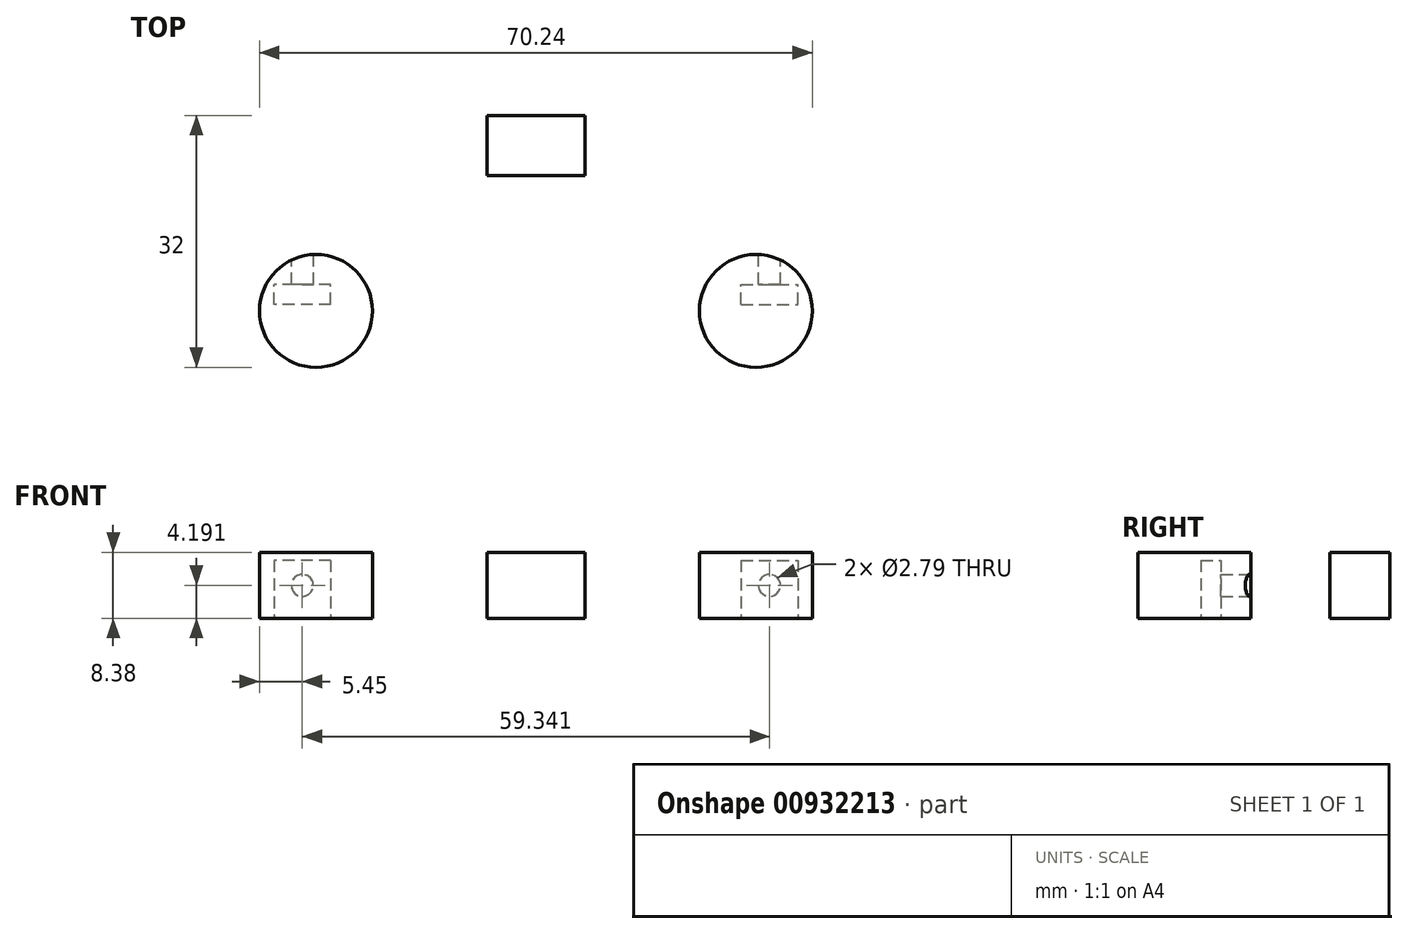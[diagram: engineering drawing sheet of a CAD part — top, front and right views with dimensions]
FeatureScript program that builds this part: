
annotation { "Feature Type Name" : "Feature", "Feature Type Description" : "" }
export const myFeature = defineFeature(function(context is Context, id is Id, definition is map)
    precondition{}
    {
        {
            var Q0;
            Q0=qCreatedBy(makeId("Top.planeOp"),FACE);
            var sketch = newSketch(context, id + "F0", { "sketchPlane" : qUnion([Q0])});
            skLineSegment(sketch, "E0", {"start": v(0, 0) * mm, "end": v(35.12, 0) * mm});
            skLineSegment(sketch, "E1", {"start": v(0, 0) * mm, "end": v(-35.12, 0) * mm});
            skLineSegment(sketch, "E2", {"start": v(0, 0) * mm, "end": v(0, -32) * mm});
            skLineSegment(sketch, "E3", {"start": v(0, 0) * mm, "end": v(0, -14.48) * mm});
            skLineSegment(sketch, "E4", {"start": v(0, -14.48) * mm, "end": v(-34.5, -14.48) * mm});
            skLineSegment(sketch, "E5", {"start": v(0, -14.48) * mm, "end": v(34.5, -14.48) * mm});
            skLineSegment(sketch, "E6", {"start": v(35.12, 0) * mm, "end": v(35.12, -32) * mm});
            skLineSegment(sketch, "E7", {"start": v(-35.12, 0) * mm, "end": v(-35.12, -32) * mm});
            skLineSegment(sketch, "E8", {"start": v(-35.12, -32) * mm, "end": v(35.12, -32) * mm});
            skLineSegment(sketch, "E9", {"start": v(-34.5, -14.48) * mm, "end": v(-35.12, -14.48) * mm});
            skLineSegment(sketch, "E10", {"start": v(-35.12, -14.48) * mm, "end": v(-35.12, -13.82) * mm});
            skLineSegment(sketch, "E11", {"start": v(-35.12, -14.48) * mm, "end": v(-35.12, -15.14) * mm});
            skLineSegment(sketch, "E12", {"start": v(-35.12, -13.82) * mm, "end": v(-34.5, -14.48) * mm});
            skLineSegment(sketch, "E13", {"start": v(-35.12, -15.14) * mm, "end": v(-34.5, -14.48) * mm});
            skLineSegment(sketch, "E14", {"start": v(35.12, -15.14) * mm, "end": v(34.5, -14.48) * mm});
            skLineSegment(sketch, "E15", {"start": v(34.5, -14.48) * mm, "end": v(35.12, -13.82) * mm});
            skLineSegment(sketch, "E16", {"start": v(35.12, -13.82) * mm, "end": v(35.12, -14.48) * mm});
            skLineSegment(sketch, "E17", {"start": v(35.12, -14.48) * mm, "end": v(35.12, -15.14) * mm});
            skLineSegment(sketch, "E18", {"start": v(0, -32) * mm, "end": v(-27.94, -32) * mm});
            skLineSegment(sketch, "E19", {"start": v(0, -32) * mm, "end": v(27.94, -32) * mm});
            skLineSegment(sketch, "E20", {"start": v(-27.94, -32) * mm, "end": v(-27.94, -24.83) * mm});
            skLineSegment(sketch, "E21", {"start": v(27.94, -32) * mm, "end": v(27.94, -24.83) * mm});
            skCircle(sketch, "E22", {"center": v(-27.94, -24.83) * mm, "radius": 7.18 * mm});
            skCircle(sketch, "E23", {"center": v(27.94, -24.83) * mm, "radius": 7.18 * mm});
            skLineSegment(sketch, "E24", {"start": v(0, 0) * mm, "end": v(-6.22, 0) * mm});
            skLineSegment(sketch, "E25", {"start": v(0, 0) * mm, "end": v(6.22, 0) * mm});
            skLineSegment(sketch, "E26", {"start": v(-6.22, 0) * mm, "end": v(-6.22, -7.62) * mm});
            skLineSegment(sketch, "E27", {"start": v(-6.22, -7.62) * mm, "end": v(6.22, -7.62) * mm});
            skLineSegment(sketch, "E28.bottom", {"start": v(6.22, 0) * mm, "end": v(-6.22, 0) * mm});
            skLineSegment(sketch, "E28.top", {"start": v(6.22, -7.62) * mm, "end": v(-6.22, -7.62) * mm});
            skLineSegment(sketch, "E28.left", {"start": v(6.22, 0) * mm, "end": v(6.22, -7.62) * mm});
            skSolve(sketch);
        }
        {
            var Q0;
            {var subQ1=sQuery(id+"F0.wireOp",EDGE,"E1");Q0=makeQuery(id+"F0.imprint","IMPRINT",FACE,{"disambiguationData":[TD([[makeQuery(id+"F0.imprint","IMPRINT",EDGE,{"derivedFrom":subQ1}),1.0]])]});}
            var Q1;
            {var subQ1=sQuery(id+"F0.wireOp",EDGE,"E0");Q1=makeQuery(id+"F0.imprint","IMPRINT",FACE,{"disambiguationData":[TD([[makeQuery(id+"F0.imprint","IMPRINT",EDGE,{"derivedFrom":subQ1}),-1.0]])]});}
            extrude(context, id + "F1", {"entities" : qUnion([Q0, Q1]), "depth" : 8.38 * mm, "offsetDistance" : 25.4 * mm});
        }
        {
            var Q0;
            Q0=makeQuery(id+"F0.imprint","IMPRINT",FACE,{"disambiguationData":[TD([[makeQuery(id+"F0.imprint","IMPRINT",EDGE,{"derivedFrom":sQuery(id+"F0.wireOp",EDGE,"E2")}),-1.0]])]});
            var Q1;
            {var subQ0=sQuery(id+"F0.wireOp",EDGE,"E22");var subQ2=makeQuery(id+"F0.imprint","INTERSECT",VERTEX,{"derivedFrom":[sQuery(id+"F0.wireOp",EDGE,"E7"),subQ0]});Q1=makeQuery(id+"F0.imprint","IMPRINT",FACE,{"disambiguationData":[TD([[makeQuery(id+"F0.imprint","IMPRINT",EDGE,{"disambiguationData":[TD([[subQ2,-1.0]])],"derivedFrom":subQ0}),1.0]])]});}
            var Q2;
            Q2=makeQuery(id+"F0.imprint","IMPRINT",FACE,{"disambiguationData":[TD([[makeQuery(id+"F0.imprint","IMPRINT",EDGE,{"derivedFrom":sQuery(id+"F0.wireOp",EDGE,"E2")}),1.0]])]});
            var Q3;
            {var subQ0=sQuery(id+"F0.wireOp",EDGE,"E23");var subQ2=makeQuery(id+"F0.imprint","INTERSECT",VERTEX,{"derivedFrom":[sQuery(id+"F0.wireOp",EDGE,"E6"),subQ0]});Q3=makeQuery(id+"F0.imprint","IMPRINT",FACE,{"disambiguationData":[TD([[makeQuery(id+"F0.imprint","IMPRINT",EDGE,{"disambiguationData":[TD([[subQ2,-1.0]])],"derivedFrom":subQ0}),1.0]])]});}
            extrude(context, id + "F2", {"entities" : qUnion([Q0, Q1, Q2, Q3]), "depth" : 8.38 * mm, "offsetDistance" : 25.4 * mm});
        }
        {
            var Q0;
            Q0=makeQuery(id+"F1.opExtrude","CAP_FACE",FACE,{"disambiguationData":[OSD([sQuery(id+"F0.wireOp",EDGE,"E0"),sQuery(id+"F0.wireOp",EDGE,"E1"),sQuery(id+"F0.wireOp",EDGE,"E4"),sQuery(id+"F0.wireOp",EDGE,"E5"),sQuery(id+"F0.wireOp",EDGE,"E6"),sQuery(id+"F0.wireOp",EDGE,"E7"),sQuery(id+"F0.wireOp",EDGE,"E12"),sQuery(id+"F0.wireOp",EDGE,"E15"),sQuery(id+"F0.wireOp",EDGE,"E28.top"),sQuery(id+"F0.wireOp",EDGE,"E28.left"),sQuery(id+"F0.wireOp",EDGE,"E26")])],"isStart":false});
            var sketch = newSketch(context, id + "F3", { "sketchPlane" : qUnion([Q0])});
            skLineSegment(sketch, "E29", {"start": v(0, -14.48) * mm, "end": v(0, 0) * mm});
            skLineSegment(sketch, "E30", {"start": v(0, 0) * mm, "end": v(35.12, 0) * mm});
            skLineSegment(sketch, "E31", {"start": v(17.56, 0) * mm, "end": v(17.56, -14.48) * mm});
            skLineSegment(sketch, "E32", {"start": v(17.56, -14.48) * mm, "end": v(0, -14.48) * mm});
            skLineSegment(sketch, "E33", {"start": v(35.12, 0) * mm, "end": v(35.12, -14.48) * mm});
            skLineSegment(sketch, "E34", {"start": v(35.12, -14.48) * mm, "end": v(17.56, -14.48) * mm});
            skLineSegment(sketch, "E35", {"start": v(17.56, -14.48) * mm, "end": v(24.23, -14.48) * mm});
            skLineSegment(sketch, "E36", {"start": v(17.56, -14.48) * mm, "end": v(10.9, -14.48) * mm});
            skLineSegment(sketch, "E37", {"start": v(10.9, -14.48) * mm, "end": v(10.9, -11.6) * mm});
            skLineSegment(sketch, "E38", {"start": v(24.23, -14.48) * mm, "end": v(24.23, -17.35) * mm});
            skLineSegment(sketch, "E39.bottom", {"start": v(10.9, -11.6) * mm, "end": v(24.23, -11.6) * mm});
            skLineSegment(sketch, "E39.top", {"start": v(10.9, -17.35) * mm, "end": v(24.23, -17.35) * mm});
            skLineSegment(sketch, "E39.left", {"start": v(10.9, -11.6) * mm, "end": v(10.9, -17.35) * mm});
            skLineSegment(sketch, "E39.right", {"start": v(24.23, -11.6) * mm, "end": v(24.23, -17.35) * mm});
            skSolve(sketch);
        }
        {
            var Q0;
            {var subQ5=sQuery(id+"F3.wireOp",EDGE,"E37");Q0=makeQuery(id+"F3.imprint","IMPRINT",FACE,{"disambiguationData":[TD([[makeQuery(id+"F3.imprint","IMPRINT",EDGE,{"derivedFrom":subQ5}),-1.0]])]});}
            var Q1;
            {var subQ5=sQuery(id+"F3.wireOp",EDGE,"E39.right");Q1=makeQuery(id+"F3.imprint","IMPRINT",FACE,{"disambiguationData":[TD([[makeQuery(id+"F3.imprint","IMPRINT",EDGE,{"derivedFrom":subQ5}),-1.0]])]});}
            var Q2;
            {var subQ4=sQuery(id+"F3.wireOp",EDGE,"E38");Q2=makeQuery(id+"F3.imprint","IMPRINT",FACE,{"disambiguationData":[TD([[makeQuery(id+"F3.imprint","IMPRINT",EDGE,{"derivedFrom":subQ4}),-1.0]])]});}
            var Q3;
            Q3=makeQuery(id+"F2.opExtrude","CAP_FACE",FACE,{"disambiguationData":[OSD([sQuery(id+"F0.wireOp",EDGE,"E4"),sQuery(id+"F0.wireOp",EDGE,"E5"),sQuery(id+"F0.wireOp",EDGE,"E6"),sQuery(id+"F0.wireOp",EDGE,"E7"),sQuery(id+"F0.wireOp",EDGE,"E13"),sQuery(id+"F0.wireOp",EDGE,"E14"),sQuery(id+"F0.wireOp",EDGE,"E18"),sQuery(id+"F0.wireOp",EDGE,"E19"),sQuery(id+"F0.wireOp",EDGE,"E22"),sQuery(id+"F0.wireOp",EDGE,"E23")])],"isStart":true});
            extrude(context, id + "F4", {"entities" : qUnion([Q0, Q1, Q2]), "operationType" : NewBodyOperationType.REMOVE, "oppositeDirection" : true, "depth" : 25.4 * mm, "endBoundEntityFace" : qUnion([Q3]), "offsetDistance" : 25.4 * mm});
        }
        {
            var Q0;
            Q0=qCreatedBy(makeId("Top.planeOp"),FACE);
            var sketch = newSketch(context, id + "F5", { "sketchPlane" : qUnion([Q0])});
            skLineSegment(sketch, "E40", {"start": v(0, 0) * mm, "end": v(35.12, 0) * mm});
            skLineSegment(sketch, "E41", {"start": v(17.56, 0) * mm, "end": v(17.56, -14.48) * mm});
            skLineSegment(sketch, "E42", {"start": v(17.56, -14.48) * mm, "end": v(24.23, -14.48) * mm});
            skLineSegment(sketch, "E43", {"start": v(35.12, 0) * mm, "end": v(35.12, -14.48) * mm});
            skLineSegment(sketch, "E44", {"start": v(35.12, -14.48) * mm, "end": v(24.23, -14.48) * mm});
            skLineSegment(sketch, "E45", {"start": v(24.23, -14.48) * mm, "end": v(35.12, -14.48) * mm});
            skLineSegment(sketch, "E46", {"start": v(29.67, -14.48) * mm, "end": v(29.67, -4.95) * mm});
            skLineSegment(sketch, "E47", {"start": v(29.67, -14.48) * mm, "end": v(29.67, -24) * mm});
            skLineSegment(sketch, "E48", {"start": v(29.67, -24) * mm, "end": v(26.05, -24) * mm});
            skLineSegment(sketch, "E49", {"start": v(29.67, -24) * mm, "end": v(29.67, -21.46) * mm});
            skLineSegment(sketch, "E50.bottom", {"start": v(26.05, -24) * mm, "end": v(33.29, -24) * mm});
            skLineSegment(sketch, "E50.top", {"start": v(26.05, -21.46) * mm, "end": v(33.29, -21.46) * mm});
            skLineSegment(sketch, "E50.left", {"start": v(26.05, -24) * mm, "end": v(26.05, -21.46) * mm});
            skLineSegment(sketch, "E50.right", {"start": v(33.29, -24) * mm, "end": v(33.29, -21.46) * mm});
            skPoint(sketch, "E50.middle", {"position": v(29.67, -22.73) * mm});
            skLineSegment(sketch, "E51", {"start": v(29.67, -22.73) * mm, "end": v(0, -22.73) * mm});
            skLineSegment(sketch, "E52", {"start": v(0, -22.73) * mm, "end": v(-29.67, -22.73) * mm});
            skLineSegment(sketch, "E53", {"start": v(26.05, -24) * mm, "end": v(0, -24) * mm});
            skLineSegment(sketch, "E54", {"start": v(0, -24) * mm, "end": v(-26.05, -24) * mm});
            skLineSegment(sketch, "E55.bottom", {"start": v(-26.05, -24) * mm, "end": v(-33.29, -24) * mm});
            skLineSegment(sketch, "E55.top", {"start": v(-26.05, -21.46) * mm, "end": v(-33.29, -21.46) * mm});
            skLineSegment(sketch, "E55.left", {"start": v(-26.05, -24) * mm, "end": v(-26.05, -21.46) * mm});
            skLineSegment(sketch, "E55.right", {"start": v(-33.29, -24) * mm, "end": v(-33.29, -21.46) * mm});
            skPoint(sketch, "E55.middle", {"position": v(-29.67, -22.73) * mm});
            skLineSegment(sketch, "E56", {"start": v(29.67, -4.95) * mm, "end": v(29.67, 0) * mm});
            skSolve(sketch);
        }
        {
            var Q0;
            {var subQ4=sQuery(id+"F5.wireOp",EDGE,"E50.bottom");Q0=makeQuery(id+"F5.imprint","IMPRINT",FACE,{"disambiguationData":[TD([[makeQuery(id+"F5.imprint","IMPRINT",EDGE,{"derivedFrom":subQ4}),1.0]])]});}
            var Q1;
            {var subQ0=sQuery(id+"F5.wireOp",EDGE,"E50.top");var subQ1=sQuery(id+"F5.wireOp",EDGE,"E47");var subQ2=makeQuery(id+"F5.imprint","INTERSECT",VERTEX,{"derivedFrom":[subQ1,subQ0]});Q1=makeQuery(id+"F5.imprint","IMPRINT",FACE,{"disambiguationData":[TD([[makeQuery(id+"F5.imprint","IMPRINT",EDGE,{"disambiguationData":[TD([[subQ2,-1.0]])],"derivedFrom":subQ1}),-1.0]])]});}
            var Q2;
            {var subQ0=sQuery(id+"F5.wireOp",EDGE,"E48");Q2=makeQuery(id+"F5.imprint","IMPRINT",FACE,{"disambiguationData":[TD([[makeQuery(id+"F5.imprint","IMPRINT",EDGE,{"derivedFrom":subQ0}),-1.0]])]});}
            var Q3;
            {var subQ1=sQuery(id+"F5.wireOp",EDGE,"E55.bottom");Q3=makeQuery(id+"F5.imprint","IMPRINT",FACE,{"disambiguationData":[TD([[makeQuery(id+"F5.imprint","IMPRINT",EDGE,{"derivedFrom":subQ1}),-1.0]])]});}
            extrude(context, id + "F6", {"entities" : qUnion([Q0, Q1, Q2, Q3]), "operationType" : NewBodyOperationType.REMOVE, "depth" : 7.37 * mm, "offsetDistance" : 25.4 * mm});
        }
        {
            var Q0;
            Q0=makeQuery(id+"F1.opExtrude","SWEPT_FACE",FACE,{"disambiguationData":[OSD([sQuery(id+"F0.wireOp",EDGE,"E0")])]});
            var sketch = newSketch(context, id + "F7", { "sketchPlane" : qUnion([Q0])});
            skLineSegment(sketch, "E57", {"start": v(-35.12, 0) * mm, "end": v(-29.67, 0) * mm});
            skLineSegment(sketch, "E58", {"start": v(-29.67, 0) * mm, "end": v(-29.67, 8.38) * mm});
            skCircle(sketch, "E59", {"center": v(-29.67, 4.2) * mm, "radius": 1.4 * mm});
            skLineSegment(sketch, "E60", {"start": v(-29.67, 4.2) * mm, "end": v(0, 4.2) * mm});
            skLineSegment(sketch, "E61", {"start": v(0, 4.2) * mm, "end": v(29.67, 4.2) * mm});
            skCircle(sketch, "E62", {"center": v(29.67, 4.2) * mm, "radius": 1.4 * mm});
            skCircle(sketch, "E63", {"center": v(-29.67, 4.2) * mm, "radius": 2.67 * mm});
            skCircle(sketch, "E64", {"center": v(29.67, 4.2) * mm, "radius": 2.67 * mm});
            skSolve(sketch);
        }
        {
            var Q0;
            {var subQ0=sQuery(id+"F7.wireOp",EDGE,"E60");var subQ1=sQuery(id+"F7.wireOp",EDGE,"E58");var subQ2=makeQuery(id+"F7.imprint","INTERSECT",VERTEX,{"derivedFrom":[subQ1,subQ0]});Q0=makeQuery(id+"F7.imprint","IMPRINT",FACE,{"disambiguationData":[TD([[makeQuery(id+"F7.imprint","IMPRINT",EDGE,{"disambiguationData":[TD([[subQ2,1.0]])],"derivedFrom":subQ1}),-1.0]])]});}
            var Q1;
            {var subQ0=sQuery(id+"F7.wireOp",EDGE,"E60");var subQ1=sQuery(id+"F7.wireOp",EDGE,"E58");var subQ2=makeQuery(id+"F7.imprint","INTERSECT",VERTEX,{"derivedFrom":[subQ1,subQ0]});Q1=makeQuery(id+"F7.imprint","IMPRINT",FACE,{"disambiguationData":[TD([[makeQuery(id+"F7.imprint","IMPRINT",EDGE,{"disambiguationData":[TD([[subQ2,-1.0]])],"derivedFrom":subQ1}),-1.0]])]});}
            var Q2;
            {var subQ0=sQuery(id+"F7.wireOp",EDGE,"E58");var subQ1=makeQuery(id+"F7.imprint","INTERSECT",VERTEX,{"derivedFrom":[subQ0,sQuery(id+"F7.wireOp",EDGE,"E60")]});Q2=makeQuery(id+"F7.imprint","IMPRINT",FACE,{"disambiguationData":[TD([[makeQuery(id+"F7.imprint","IMPRINT",EDGE,{"disambiguationData":[TD([[subQ1,1.0]])],"derivedFrom":subQ0}),1.0]])]});}
            var Q3;
            Q3=makeQuery(id+"F7.imprint","IMPRINT",FACE,{"disambiguationData":[TD([[makeQuery(id+"F7.imprint","IMPRINT",EDGE,{"derivedFrom":sQuery(id+"F7.wireOp",EDGE,"E62")}),1.0]])]});
            extrude(context, id + "F8", {"entities" : qUnion([Q0, Q1, Q2, Q3]), "operationType" : NewBodyOperationType.REMOVE, "oppositeDirection" : true, "depth" : 24 * mm, "offsetDistance" : 25.4 * mm});
        }
        {
            var Q0;
            {var subQ0=sQuery(id+"F7.wireOp",EDGE,"E59");var subQ1=sQuery(id+"F7.wireOp",EDGE,"E58");var subQ2=makeQuery(id+"F7.imprint","INTERSECT",VERTEX,{"disambiguationData":[OD(1.0)],"derivedFrom":[subQ1,subQ0]});Q0=makeQuery(id+"F7.imprint","IMPRINT",FACE,{"disambiguationData":[TD([[makeQuery(id+"F7.imprint","IMPRINT",EDGE,{"disambiguationData":[TD([[subQ2,-1.0]])],"derivedFrom":subQ1}),-1.0]])]});}
            var Q1;
            {var subQ0=sQuery(id+"F7.wireOp",EDGE,"E63");var subQ1=sQuery(id+"F7.wireOp",EDGE,"E58");var subQ2=makeQuery(id+"F7.imprint","INTERSECT",VERTEX,{"disambiguationData":[OD(0.0)],"derivedFrom":[subQ1,subQ0]});Q1=makeQuery(id+"F7.imprint","IMPRINT",FACE,{"disambiguationData":[TD([[makeQuery(id+"F7.imprint","IMPRINT",EDGE,{"disambiguationData":[TD([[subQ2,-1.0]])],"derivedFrom":subQ1}),1.0]])]});}
            var Q2;
            {var subQ0=sQuery(id+"F7.wireOp",EDGE,"E63");var subQ1=sQuery(id+"F7.wireOp",EDGE,"E58");var subQ2=makeQuery(id+"F7.imprint","INTERSECT",VERTEX,{"disambiguationData":[OD(0.0)],"derivedFrom":[subQ1,subQ0]});Q2=makeQuery(id+"F7.imprint","IMPRINT",FACE,{"disambiguationData":[TD([[makeQuery(id+"F7.imprint","IMPRINT",EDGE,{"disambiguationData":[TD([[subQ2,-1.0]])],"derivedFrom":subQ1}),-1.0]])]});}
            var Q3;
            Q3=makeQuery(id+"F7.imprint","IMPRINT",FACE,{"disambiguationData":[TD([[makeQuery(id+"F7.imprint","IMPRINT",EDGE,{"derivedFrom":sQuery(id+"F7.wireOp",EDGE,"E62")}),-1.0]])]});
            extrude(context, id + "F9", {"entities" : qUnion([Q0, Q1, Q2, Q3]), "operationType" : NewBodyOperationType.REMOVE, "oppositeDirection" : true, "depth" : 4.95 * mm, "offsetDistance" : 25.4 * mm});
        }
        {
            var Q0;
            Q0=makeQuery(id+"F2.opExtrude","CAP_FACE",FACE,{"disambiguationData":[OSD([sQuery(id+"F0.wireOp",EDGE,"E4"),sQuery(id+"F0.wireOp",EDGE,"E5"),sQuery(id+"F0.wireOp",EDGE,"E6"),sQuery(id+"F0.wireOp",EDGE,"E7"),sQuery(id+"F0.wireOp",EDGE,"E13"),sQuery(id+"F0.wireOp",EDGE,"E14"),sQuery(id+"F0.wireOp",EDGE,"E18"),sQuery(id+"F0.wireOp",EDGE,"E19"),sQuery(id+"F0.wireOp",EDGE,"E22"),sQuery(id+"F0.wireOp",EDGE,"E23")])],"isStart":false});
            var sketch = newSketch(context, id + "F10", { "sketchPlane" : qUnion([Q0])});
            skLineSegment(sketch, "E65", {"start": v(10.9, -14.48) * mm, "end": v(24.23, -14.48) * mm});
            skLineSegment(sketch, "E66", {"start": v(17.56, -14.48) * mm, "end": v(10.32, -14.48) * mm});
            skLineSegment(sketch, "E67", {"start": v(17.56, -14.48) * mm, "end": v(24.8, -14.48) * mm});
            skLineSegment(sketch, "E68", {"start": v(17.56, -14.48) * mm, "end": v(17.56, -18.03) * mm});
            skLineSegment(sketch, "E69", {"start": v(17.56, -14.48) * mm, "end": v(17.56, -10.92) * mm});
            skLineSegment(sketch, "E70", {"start": v(17.56, -10.92) * mm, "end": v(11.72, -10.92) * mm});
            skLineSegment(sketch, "E71", {"start": v(17.56, -18.03) * mm, "end": v(23.4, -18.03) * mm});
            skLineSegment(sketch, "E72.bottom", {"start": v(11.72, -10.92) * mm, "end": v(23.4, -10.92) * mm});
            skLineSegment(sketch, "E72.top", {"start": v(11.72, -18.03) * mm, "end": v(23.4, -18.03) * mm});
            skLineSegment(sketch, "E72.left", {"start": v(11.72, -10.92) * mm, "end": v(11.72, -18.03) * mm});
            skLineSegment(sketch, "E72.right", {"start": v(23.4, -10.92) * mm, "end": v(23.4, -18.03) * mm});
            skPoint(sketch, "E72.middle", {"position": v(17.56, -14.48) * mm});
            skLineSegment(sketch, "E73", {"start": v(24.8, -14.48) * mm, "end": v(24.8, -16.38) * mm});
            skLineSegment(sketch, "E74.bottom", {"start": v(24.8, -16.38) * mm, "end": v(10.32, -16.38) * mm});
            skLineSegment(sketch, "E74.top", {"start": v(24.8, -12.57) * mm, "end": v(10.32, -12.57) * mm});
            skLineSegment(sketch, "E74.left", {"start": v(24.8, -16.38) * mm, "end": v(24.8, -12.57) * mm});
            skLineSegment(sketch, "E74.right", {"start": v(10.32, -16.38) * mm, "end": v(10.32, -12.57) * mm});
            skSolve(sketch);
        }
        {
            var Q0;
            {var subQ7=sQuery(id+"F10.wireOp",EDGE,"E66");Q0=makeQuery(id+"F10.imprint","IMPRINT",FACE,{"disambiguationData":[TD([[makeQuery(id+"F10.imprint","IMPRINT",EDGE,{"derivedFrom":subQ7}),-1.0]])]});}
            var Q1;
            {var subQ0=sQuery(id+"F10.wireOp",EDGE,"E72.bottom");Q1=makeQuery(id+"F10.imprint","IMPRINT",FACE,{"disambiguationData":[TD([[makeQuery(id+"F10.imprint","IMPRINT",EDGE,{"derivedFrom":subQ0}),-1.0]])]});}
            var Q2;
            {var subQ6=sQuery(id+"F10.wireOp",EDGE,"E67");Q2=makeQuery(id+"F10.imprint","IMPRINT",FACE,{"disambiguationData":[TD([[makeQuery(id+"F10.imprint","IMPRINT",EDGE,{"derivedFrom":subQ6}),-1.0]])]});}
            var Q3;
            {var subQ0=sQuery(id+"F10.wireOp",EDGE,"E67");Q3=makeQuery(id+"F10.imprint","IMPRINT",FACE,{"disambiguationData":[TD([[makeQuery(id+"F10.imprint","IMPRINT",EDGE,{"derivedFrom":subQ0}),1.0]])]});}
            var Q4;
            {var subQ0=sQuery(id+"F10.wireOp",EDGE,"E66");Q4=makeQuery(id+"F10.imprint","IMPRINT",FACE,{"disambiguationData":[TD([[makeQuery(id+"F10.imprint","IMPRINT",EDGE,{"derivedFrom":subQ0}),1.0]])]});}
            var Q5;
            {var subQ0=sQuery(id+"F10.wireOp",EDGE,"E72.top");Q5=makeQuery(id+"F10.imprint","IMPRINT",FACE,{"disambiguationData":[TD([[makeQuery(id+"F10.imprint","IMPRINT",EDGE,{"derivedFrom":subQ0}),1.0]])]});}
            var Q6;
            {var subQ0=sQuery(id+"F10.wireOp",EDGE,"E71");Q6=makeQuery(id+"F10.imprint","IMPRINT",FACE,{"disambiguationData":[TD([[makeQuery(id+"F10.imprint","IMPRINT",EDGE,{"derivedFrom":subQ0}),1.0]])]});}
            var Q7;
            {var subQ0=sQuery(id+"F10.wireOp",EDGE,"E70");Q7=makeQuery(id+"F10.imprint","IMPRINT",FACE,{"disambiguationData":[TD([[makeQuery(id+"F10.imprint","IMPRINT",EDGE,{"derivedFrom":subQ0}),1.0]])]});}
            extrude(context, id + "F11", {"entities" : qUnion([Q0, Q1, Q2, Q3, Q4, Q5, Q6, Q7]), "operationType" : NewBodyOperationType.REMOVE, "oppositeDirection" : true, "depth" : 0.5 * mm, "offsetDistance" : 25.4 * mm});
        }
    });
